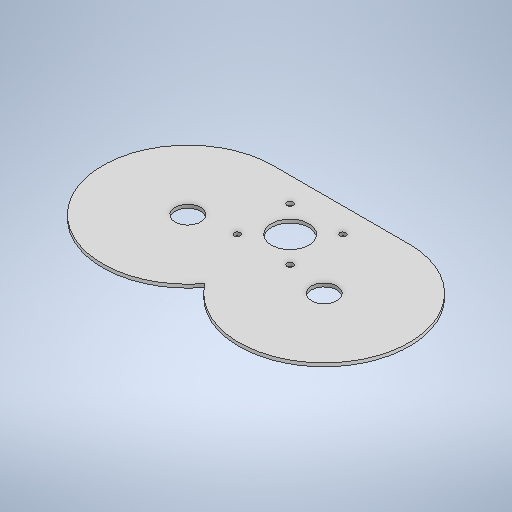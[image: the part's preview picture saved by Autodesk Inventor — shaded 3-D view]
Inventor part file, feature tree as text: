
AUTODESK INVENTOR PART (.ipt)
format: ipt  version: 2025.2 (Build 292293000, 293)  size: 248,320 bytes
history: native  units: mm
features: extrude x1, sketch x1
ambient origin geometry x8: Origin, YZ Plane, XZ Plane, XY Plane, X Axis, Y Axis, Z Axis, Center Point
bodies: Solid1 (feature_tree)
feature tree (2):
  extrude  "Extrusion1"  Depth=2.0mm
  sketch  "Sketch1"  dims[d0=80.0mm d1=15.0mm d2=15.0mm d3=100.0mm d4=100.0mm d5=14.5mm d6=31.0mm d7=31.0mm d8=3.6mm d9=3.6mm d10=3.6mm d11=3.6mm d12=2.0mm d13=0.0mm d14=22.0mm]
